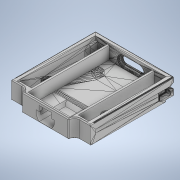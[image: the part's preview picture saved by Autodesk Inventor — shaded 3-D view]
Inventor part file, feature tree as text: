
AUTODESK INVENTOR PART (.ipt)
format: ipt  version: 2022 (Build 260153000, 153)  size: 2,708,480 bytes
history: native  units: in
note: dims shown in document units (in); Inventor stores cm internally (conversion verified against a paired STEP export)
features: extrude x11, sketch x11, fillet x1, chamfer x1, other x1
ambient origin geometry x8: Origin, YZ Plane, XZ Plane, XY Plane, X Axis, Y Axis, Z Axis, Center Point
bodies: Solid1 (feature_tree)
feature tree (25):
  extrude  "Extrusion1"  Depth=0.2638in
  extrude  "Extrusion5"  Depth=0.3225in
  extrude  "Extrusion6"  Depth=0.0295in
  extrude  "Extrusion7"  TaperAngle=90.0deg  [1 undecoded]
  extrude  "Extrusion8"  Depth=0.3937in TaperAngle=0.0deg
  extrude  "Extrusion4"  Depth=0.0839in TaperAngle=0.0deg
  extrude  "Extrusion11"  Depth=0.0394in
  extrude  "Extrusion12"  Depth=0.3937in TaperAngle=0.0deg
  extrude  "Extrusion13"  Depth=0.0197in
  fillet  "Fillet3"  Radius=0.3937in
  extrude  "Extrusion14"  Depth=0.3937in TaperAngle=0.0deg
  chamfer  "Chamfer2"  Distance=0.0492in Angle=45.0deg
  extrude  "Extrusion15"  [1 undecoded]
  sketch  "Sketch1"  dims[d0=0.0591in d1=0.0in d26=0.2638in]
  sketch  "Sketch11"  dims[d34=0.3225in d35=0.3225in]
  sketch  "Sketch12"  dims[d36=0.0295in d39=0.0295in]
  sketch  "Sketch13"  dims[d40=0.0295in d41=90.0deg]
  sketch  "Sketch14"  dims[d42=0.0295in d43=0.3937in d44=0.0in]
  sketch  "Sketch16"  dims[d58=0.0197in d59=0.0in d60=0.0839in d61=0.0in]
  sketch  "Sketch20"  dims[d66=0.0839in d67=0.0in d68=0.0394in]
  sketch  "Sketch21"  dims[d69=0.0197in d70=0.0in d77=0.3937in d78=0.0in]
  sketch  "Sketch22"  dims[d82=0.3937in d83=0.0in d84=0.0197in d85=0.3937in d86=0.0in]
  sketch  "Sketch24"  dims[d87=0.0118in d90=0.3937in d91=0.0in d93=0.0492in d94=0.0453in d95=45.0deg]
  sketch  "Sketch25"  dims[d96=0.3937in d97=0.0in]
  other  "expansionCardSelf-tappingBulkyLugs"
note: 2 required parameter values undecoded (feature->parameter linkage not recoverable at this tier; creation-order binding heuristic only, values carry confidence <= 0.55)
